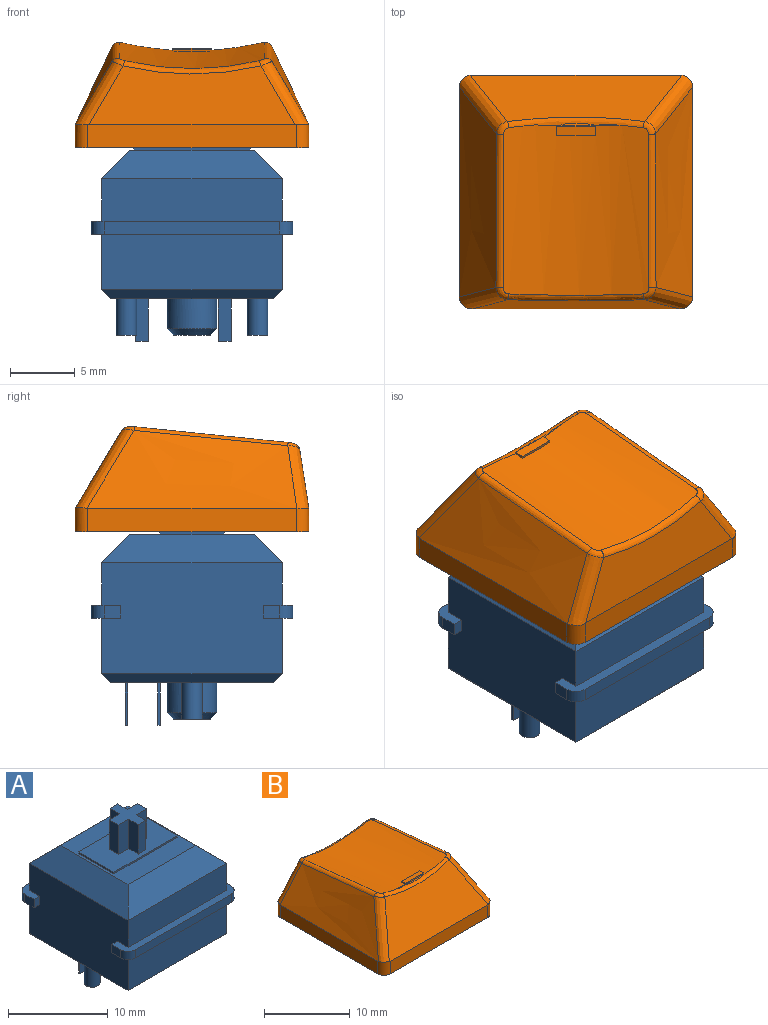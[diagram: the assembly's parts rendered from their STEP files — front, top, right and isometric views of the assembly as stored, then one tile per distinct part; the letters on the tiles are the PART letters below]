
ASSEMBLY  parts=2 mates=1
PART A: 69 faces, bbox 15.6x15.6x18.6 mm
  f0: plane 15.6x2.3mm, normal (0,0,-1), area 14.4mm2, adj f2,f3,f28,f30,f35,f60,f62,f63
  f1: plane 15.6x2.3mm, normal (0,0,-1), area 14.4mm2, adj f28,f30,f33,f34,f36,f59,f61,f64
  f2: plane 1.3x1mm, normal (1,0,0), area 1.3mm2, adj f0,f32,f62,f66
  f3: plane 1.3x1mm, normal (-1,0,0), area 1.3mm2, adj f0,f32,f63,f68
  f4: plane 15.6x2.3mm, normal (0,0,1), area 14.4mm2, adj f28,f30,f31,f33,f34,f36,f61,f64
  f5: plane 14x2.2mm, normal (-0.71,0,0.71), area 36.7mm2, adj f6,f7,f26,f30
  f6: plane 14x2.2mm, normal (0,-0.71,0.71), area 36.7mm2, adj f5,f7,f27,f31
  f7: plane 9.6x9.6mm, normal (0,0,1), area 47.2mm2, adj f5,f6,f8,f9,f10,f11,f26,f27
  f8: plane 5x0.2mm, normal (1,0,0), area 1mm2, adj f7,f9,f11,f12
  f9: plane 9x0.2mm, normal (0,1,0), area 1.8mm2, adj f7,f8,f10,f12
  f10: plane 5x0.2mm, normal (-1,0,0), area 1mm2, adj f7,f9,f11,f12
  f11: plane 9x0.2mm, normal (0,-1,0), area 1.8mm2, adj f7,f8,f10,f12
  f12: plane 9x5mm, normal (0,0,1), area 36.9mm2, adj f8,f9,f10,f11,f13,f14,f15,f16
  f13: plane 3.6x1.35mm, normal (1,0,0), area 4.9mm2, adj f12,f14,f24,f25
  f14: plane 3.6x1.08mm, normal (0,1,0), area 3.9mm2, adj f12,f13,f15,f25
  f15: plane 3.6x1.35mm, normal (-1,0,0), area 4.9mm2, adj f12,f14,f16,f25
  f16: plane 3.6x1.46mm, normal (0,1,0), area 5.3mm2, adj f12,f15,f17,f25
  f17: plane 3.6x1.3mm, normal (-1,0,0), area 4.7mm2, adj f12,f16,f18,f25
  f18: plane 3.6x1.46mm, normal (0,-1,0), area 5.3mm2, adj f12,f17,f19,f25
  f19: plane 3.6x1.35mm, normal (-1,0,0), area 4.9mm2, adj f12,f18,f20,f25
  f20: plane 3.6x1.08mm, normal (0,-1,0), area 3.9mm2, adj f12,f19,f21,f25
  f21: plane 3.6x1.35mm, normal (1,0,0), area 4.9mm2, adj f12,f20,f22,f25
  f22: plane 3.6x1.46mm, normal (0,-1,0), area 5.3mm2, adj f12,f21,f23,f25
  f23: plane 3.6x1.3mm, normal (1,0,0), area 4.7mm2, adj f12,f22,f24,f25
  f24: plane 3.6x1.46mm, normal (0,1,0), area 5.3mm2, adj f12,f13,f23,f25
  f25: plane 4x4mm, normal (0,0,1), area 8.1mm2, adj f13,f14,f15,f16,f17,f18,f19,f20
  f26: plane 14x2.2mm, normal (0,0.71,0.71), area 36.7mm2, adj f5,f7,f27,f29
  f27: plane 14x2.2mm, normal (0.71,0,0.71), area 36.7mm2, adj f6,f7,f26,f28
  f28: plane 14x8.6mm, normal (1,0,0), area 117.4mm2, adj f0,f1,f4,f27,f29,f31,f32,f55
  f29: plane 14x3.3mm, normal (0,1,0), area 46.2mm2, adj f26,f28,f30,f32
  f30: plane 14x8.6mm, normal (-1,0,0), area 117.4mm2, adj f0,f1,f4,f5,f29,f31,f32,f57
  f31: plane 14x3.3mm, normal (0,-1,0), area 46.2mm2, adj f4,f6,f28,f30
  f32: plane 15.6x2.3mm, normal (0,0,1), area 14.4mm2, adj f2,f3,f28,f29,f30,f35,f62,f63
  f33: plane 13.6x1mm, normal (0,-1,0), area 13.6mm2, adj f1,f4,f61,f64
  f34: plane 1.3x1mm, normal (1,0,0), area 1.3mm2, adj f1,f4,f61,f65
  f35: plane 13.6x1mm, normal (0,1,0), area 13.6mm2, adj f0,f32,f62,f63
  f36: plane 1.3x1mm, normal (-1,0,0), area 1.3mm2, adj f1,f4,f64,f67
  f37: plane 2.85x2.85mm, normal (0,0,-1), area 6.4mm2, adj f38
  f38: cone r=1.43mm half-angle=45deg, axis (0,0,1), area 7.4mm2, adj f37,f43
  f39: plane 1x0.2mm, normal (0,0,-1), area 0.2mm2, adj f44,f45,f46,f47
  f40: plane 1x0.2mm, normal (0,0,-1), area 0.2mm2, adj f48,f49,f50,f51
  f41: plane 1.6x1.6mm, normal (0,0,-1), area 2mm2, adj f52
  f42: plane 1.6x1.6mm, normal (0,0,-1), area 2mm2, adj f53
  f43: cylinder r=1.93mm len=3.85mm, axis (0,0,1), area 27.8mm2, adj f38,f54
  f44: plane 3.3x0.2mm, normal (-1,0,0), area 0.7mm2, adj f39,f45,f47,f54
  f45: plane 3.3x1mm, normal (0,1,0), area 3.3mm2, adj f39,f44,f46,f54
  f46: plane 3.3x0.2mm, normal (1,0,0), area 0.7mm2, adj f39,f45,f47,f54
  f47: plane 3.3x1mm, normal (0,-1,0), area 3.3mm2, adj f39,f44,f46,f54
  f48: plane 3.3x0.2mm, normal (-1,0,0), area 0.7mm2, adj f40,f49,f51,f54
  f49: plane 3.3x1mm, normal (0,1,0), area 3.3mm2, adj f40,f48,f50,f54
  f50: plane 3.3x0.2mm, normal (1,0,0), area 0.7mm2, adj f40,f49,f51,f54
  f51: plane 3.3x1mm, normal (0,-1,0), area 3.3mm2, adj f40,f48,f50,f54
  f52: cylinder r=0.8mm len=2.8mm, axis (0,0,1), area 14.1mm2, adj f41,f54
  f53: cylinder r=0.8mm len=2.8mm, axis (0,0,1), area 14.1mm2, adj f42,f54
  f54: plane 12.6x12.6mm, normal (0,0,-1), area 142.7mm2, adj f43,f44,f45,f46,f47,f48,f49,f50
  f55: plane 14x0.7mm, normal (0.71,0,-0.71), area 13.2mm2, adj f28,f54,f56,f58
  f56: plane 14x0.7mm, normal (0,0.71,-0.71), area 13.2mm2, adj f54,f55,f57,f60
  f57: plane 14x0.7mm, normal (-0.71,0,-0.71), area 13.2mm2, adj f30,f54,f56,f58
  f58: plane 14x0.7mm, normal (0,-0.71,-0.71), area 13.2mm2, adj f54,f55,f57,f59
  f59: plane 14x4.3mm, normal (0,-1,0), area 60.2mm2, adj f1,f28,f30,f58
  f60: plane 14x4.3mm, normal (0,1,0), area 60.2mm2, adj f0,f28,f30,f56
  f61: cylinder r=1mm len=1mm, axis (0,0,-1), area 1.6mm2, adj f1,f4,f33,f34
  f62: cylinder r=1mm len=1mm, axis (0,0,1), area 1.6mm2, adj f0,f2,f32,f35
  f63: cylinder r=1mm len=1mm, axis (0,0,-1), area 1.6mm2, adj f0,f3,f32,f35
  f64: cylinder r=1mm len=1mm, axis (0,0,1), area 1.6mm2, adj f1,f4,f33,f36
  f65: plane 1x0.8mm, normal (0,1,0), area 0.8mm2, adj f1,f4,f28,f34
  f66: plane 1x0.8mm, normal (0,-1,0), area 0.8mm2, adj f0,f2,f28,f32
  f67: plane 1x0.8mm, normal (0,1,0), area 0.8mm2, adj f1,f4,f30,f36
  f68: plane 1x0.8mm, normal (0,-1,0), area 0.8mm2, adj f0,f3,f30,f32
PART B: 55 faces, bbox 21.2x21.9x10.6 mm
  f0: cylinder r=22.9mm len=13.02mm, axis (0,0.99,-0.1), area 144.3mm2, adj f18,f19,f20,f21,f22,f23,f24,f25
  f1: plane 18.1x18.1mm, normal (0,0,-1), area 67.5mm2, adj f2,f3,f4,f5,f10,f12,f14,f16
  f2: plane 16.1x1.8mm, normal (1,0,0), area 29mm2, adj f1,f9,f10,f16
  f3: plane 16.1x1.8mm, normal (0,1,0), area 29mm2, adj f1,f6,f14,f15,f16,f17
  f4: plane 16.1x1.8mm, normal (-1,0,0), area 29mm2, adj f1,f7,f12,f14
  f5: plane 16.1x1.8mm, normal (0,-1,0), area 29mm2, adj f1,f8,f10,f12
  f6: plane 15.96x4.53mm, normal (0,0.99,0.15), area 56.4mm2, adj f3,f15,f17,f20
  f7: bspline ~18.1x6.49mm, area 87.4mm2, adj f4,f12,f13,f14,f15,f19
  f8: plane 16.37x6.05mm, normal (0,-0.86,0.51), area 90.2mm2, adj f5,f10,f11,f12,f13,f23
  f9: bspline ~18.1x6.49mm, area 87.4mm2, adj f2,f10,f11,f16,f17,f24
  f10: cylinder r=1mm len=1.88mm, axis (0,0,-1), area 2.9mm2, adj f1,f2,f5,f8,f9,f11
  f11: bspline ~7.99x5.46mm, area 10.4mm2, adj f8,f9,f10,f25
  f12: cylinder r=1mm len=1.88mm, axis (0,0,1), area 2.9mm2, adj f1,f4,f5,f7,f8,f13
  f13: bspline ~8.01x5.47mm, area 10.4mm2, adj f7,f8,f12,f21
  f14: cylinder r=1mm len=1.8mm, axis (0,0,-1), area 2.8mm2, adj f1,f3,f4,f7,f15
  f15: bspline ~6.46x4.4mm, area 8.2mm2, adj f3,f6,f7,f14,f18
  f16: cylinder r=1mm len=1.8mm, axis (0,0,1), area 2.8mm2, adj f1,f2,f3,f9,f17
  f17: bspline ~6.45x4.39mm, area 8.2mm2, adj f3,f6,f9,f16,f22
  f18: bspline ~1.17x1.02mm, area 0.7mm2, adj f0,f15,f19,f20
  f19: bspline ~17.37x2.1mm, area 8mm2, adj f0,f7,f18,f21
  f20: bspline ~10.64x1.03mm, area 7mm2, adj f0,f6,f18,f22
  f21: bspline ~1.13x1.07mm, area 0.7mm2, adj f0,f13,f19,f23
  f22: bspline ~1.17x1mm, area 0.7mm2, adj f0,f17,f20,f24
  f23: bspline ~10.62x0.82mm, area 6mm2, adj f0,f8,f21,f25
  f24: bspline ~17.37x2.1mm, area 8mm2, adj f0,f9,f22,f25
  f25: bspline ~1.24x1.01mm, area 0.7mm2, adj f0,f11,f23,f24
  f26: plane 16.13x1.61mm, normal (-1,0,0), area 25mm2, adj f1,f27,f29,f32,f33
  f27: plane 16.1x1.72mm, normal (0,-1,0), area 27.7mm2, adj f1,f26,f28,f30,f31,f33
  f28: plane 16.13x1.61mm, normal (1,0,0), area 25mm2, adj f1,f27,f29,f31,f32
  f29: plane 16.1x1.52mm, normal (0,1,0), area 24.5mm2, adj f1,f26,f28,f32
  f30: plane 16.21x4.45mm, normal (0,-0.99,-0.15), area 51mm2, adj f27,f31,f33,f34
  f31: offset ~20.1x8.49mm, area 78.8mm2, adj f27,f28,f30,f32,f34
  f32: plane 16.68x6.12mm, normal (0,0.86,-0.51), area 82.2mm2, adj f26,f28,f29,f31,f33,f34
  f33: offset ~20.1x8.49mm, area 78.8mm2, adj f26,f27,f30,f32,f34
  f34: cylinder r=23.9mm len=12.22mm, axis (0,0.99,-0.1), area 111.1mm2, adj f30,f31,f32,f33,f46
  f35: plane 5.88x1.35mm, normal (-1,0,0), area 7.8mm2, adj f36,f44,f45,f49
  f36: plane 5.97x1.5mm, normal (0,-1,0), area 8.9mm2, adj f35,f37,f45,f49
  f37: plane 6.1x1.3mm, normal (-1,0,0), area 7.8mm2, adj f36,f38,f45,f49
  f38: plane 6.1x1.5mm, normal (0,1,0), area 9.1mm2, adj f37,f39,f45,f49
  f39: plane 6.16x1.35mm, normal (-1,0,0), area 8.2mm2, adj f38,f40,f45,f49
  f40: plane 6.16x1mm, normal (0,1,0), area 6.2mm2, adj f39,f41,f45,f49
  f41: plane 6.16x1.35mm, normal (1,0,0), area 8.2mm2, adj f40,f42,f45,f49
  f42: plane 6.1x1.5mm, normal (0,1,0), area 9.1mm2, adj f41,f43,f45,f49
  f43: plane 6.1x1.3mm, normal (1,0,0), area 7.8mm2, adj f42,f45,f47,f49
  f44: plane 5.74x1mm, normal (0,-1,0), area 5.7mm2, adj f35,f45,f48,f49
  f45: plane 5.5x5.5mm, normal (0,0,-1), area 15.9mm2, adj f35,f36,f37,f38,f39,f40,f41,f42
  f46: cylinder r=2.75mm len=6.11mm, axis (0,0,-1), area 105.5mm2, adj f34,f45
  f47: plane 5.97x1.5mm, normal (0,-1,0), area 8.9mm2, adj f43,f45,f48,f49
  f48: plane 5.88x1.35mm, normal (1,0,0), area 7.8mm2, adj f44,f45,f47,f49
  f49: cylinder r=23.9mm len=4.01mm, axis (0,0.99,-0.1), area 7.9mm2, adj f35,f36,f37,f38,f39,f40,f41,f42
  f50: plane 0.71x0.22mm, normal (1,0,0), area 0.1mm2, adj f0,f51,f53,f54
  f51: plane 3x0.2mm, normal (0,0.99,-0.1), area 0.6mm2, adj f0,f50,f52,f54
  f52: plane 0.71x0.22mm, normal (-1,0,0), area 0.1mm2, adj f0,f51,f53,f54
  f53: plane 3x0.2mm, normal (0,-0.99,0.1), area 0.6mm2, adj f0,f50,f52,f54
  f54: plane 3x0.7mm, normal (0,0.1,0.99), area 2.1mm2, adj f50,f51,f52,f53
PLACE A at identity fixed
PLACE B rot(axis=(0,0,1),180deg) t=(0,0,11.7)mm
MATE fastened B.f46 <-> A.f38  axis (0,0,-1) through (0,0,11.7)mm
